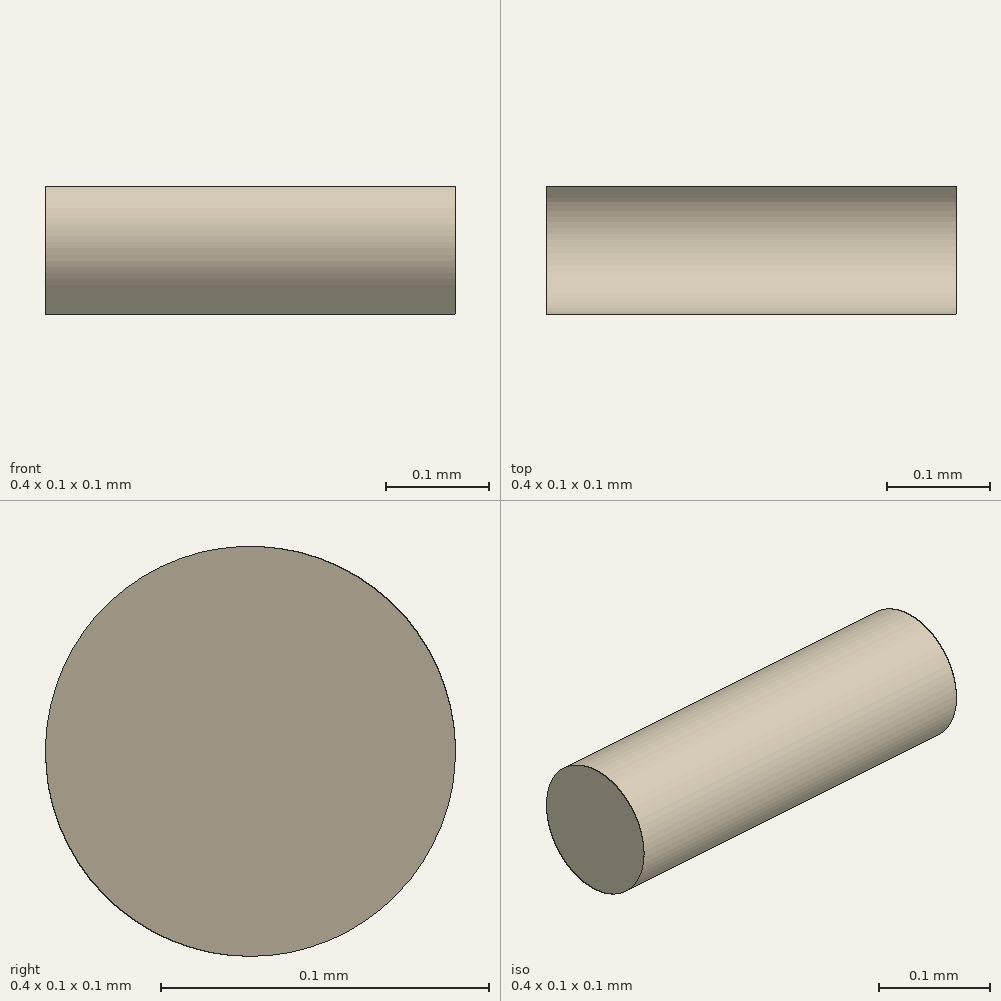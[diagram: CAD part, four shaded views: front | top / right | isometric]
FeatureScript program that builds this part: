
annotation { "Feature Type Name" : "Feature", "Feature Type Description" : "" }
export const myFeature = defineFeature(function(context is Context, id is Id, definition is map)
    precondition{}
    {
        {
            var Q0;
            Q0=qCreatedBy(makeId("Right.planeOp"),FACE);
            var sketch = newSketch(context, id + "F0", { "sketchPlane" : qUnion([Q0])});
            skCircle(sketch, "E0", {"center": v(0, 0) * mm, "radius": 0.06 * mm});
            skSolve(sketch);
        }
        {
            var Q0;
            Q0=qSketchRegion(id+"F0",true);
            extrude(context, id + "F1", {"entities" : qUnion([Q0]), "depth" : 0.4 * mm, "offsetDistance" : 25 * mm});
        }
    });
